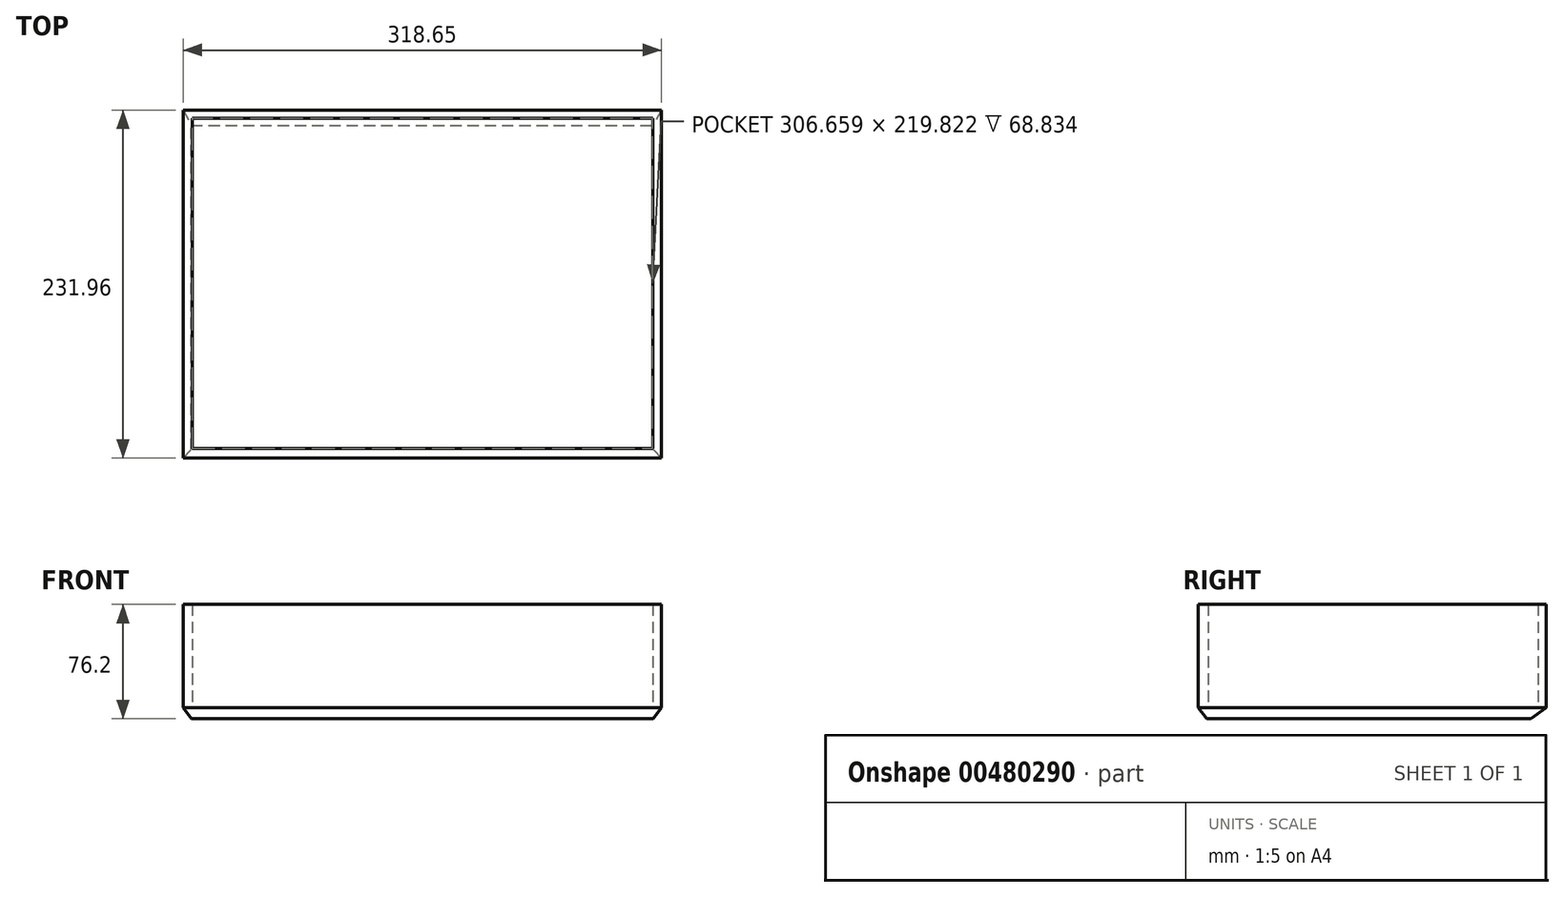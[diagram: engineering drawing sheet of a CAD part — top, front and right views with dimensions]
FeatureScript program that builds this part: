
annotation { "Feature Type Name" : "Feature", "Feature Type Description" : "" }
export const myFeature = defineFeature(function(context is Context, id is Id, definition is map)
    precondition{}
    {
        {
            var Q0;
            Q0=qCreatedBy(makeId("Top.planeOp"),FACE);
            var sketch = newSketch(context, id + "F0", { "sketchPlane" : qUnion([Q0])});
            skLineSegment(sketch, "E0", {"start": v(295, -203.38) * mm, "end": v(-12.7, -203.38) * mm});
            skPoint(sketch, "E1.end.orphan", {"position": v(-12.7, 12.7) * mm});
            skLineSegment(sketch, "E2", {"start": v(-12.7, -203.38) * mm, "end": v(-12.7, 12.7) * mm});
            skLineSegment(sketch, "E3", {"start": v(-12.7, 12.7) * mm, "end": v(295, 12.7) * mm});
            skPoint(sketch, "E4.start.orphan", {"position": v(295, -190.68) * mm});
            skLineSegment(sketch, "E5", {"start": v(295, -203.38) * mm, "end": v(295, 12.7) * mm});
            skPoint(sketch, "E6.end.orphan", {"position": v(0, -190.68) * mm});
            skPoint(sketch, "E7.end.orphan", {"position": v(282.3, -190.68) * mm});
            skPoint(sketch, "E8.start.orphan", {"position": v(0, 0) * mm});
            skSolve(sketch);
        }
        {
            var Q0;
            Q0=qCreatedBy(makeId("Top.planeOp"),FACE);
            cPlane(context, id + "F1", {"entities" : qUnion([Q0]), "cplaneType" : CPlaneType.OFFSET, "offset" : 7.37 * mm, "width" : 152.4 * mm, "height" : 152.4 * mm});
        }
        {
            var Q0;
            Q0=qCreatedBy(id+"F1.planeOp",FACE);
            var sketch = newSketch(context, id + "F2", { "sketchPlane" : qUnion([Q0])});
            skLineSegment(sketch, "E9", {"start": v(-18.2, 22.82) * mm, "end": v(300.45, 22.82) * mm});
            skLineSegment(sketch, "E10", {"start": v(300.45, 22.82) * mm, "end": v(300.45, -209.14) * mm});
            skLineSegment(sketch, "E11", {"start": v(300.45, -209.14) * mm, "end": v(-18.2, -209.14) * mm});
            skLineSegment(sketch, "E12", {"start": v(-18.2, -209.14) * mm, "end": v(-18.2, 22.82) * mm});
            skSolve(sketch);
        }
        {
            var Q0;
            Q0=makeQuery(id+"F2.imprint","IMPRINT",FACE,{"disambiguationData":[TD([[makeQuery(id+"F2.imprint","IMPRINT",EDGE,{"derivedFrom":sQuery(id+"F2.wireOp",EDGE,"E9")}),-1.0]])]});
            var Q1;
            Q1=makeQuery(id+"F0.imprint","IMPRINT",FACE,{"disambiguationData":[TD([[makeQuery(id+"F0.imprint","IMPRINT",EDGE,{"derivedFrom":sQuery(id+"F0.wireOp",EDGE,"E0")}),-1.0]])]});
            loft(context, id + "F3", {"sheetProfilesArray" : [{ "sheetProfileEntities" : qUnion([Q0]) }, { "sheetProfileEntities" : qUnion([Q1]) }]});
        }
        {
            var Q0;
            Q0=makeQuery(id+"F3.opLoft","CAP_FACE",FACE,{"disambiguationData":[OSD([makeQuery(id+"F2.imprint","IMPRINT",FACE,{"disambiguationData":[TD([[makeQuery(id+"F2.imprint","IMPRINT",EDGE,{"derivedFrom":sQuery(id+"F2.wireOp",EDGE,"E9")}),-1.0]])]})])],"isStart":true});
            var sketch = newSketch(context, id + "F4", { "sketchPlane" : qUnion([Q0])});
            skLineSegment(sketch, "E13", {"start": v(-18.2, 22.82) * mm, "end": v(-18.2, -209.14) * mm});
            skLineSegment(sketch, "E14", {"start": v(-18.2, -209.14) * mm, "end": v(300.45, -209.14) * mm});
            skLineSegment(sketch, "E15", {"start": v(300.45, -209.14) * mm, "end": v(300.45, 22.82) * mm});
            skLineSegment(sketch, "E16", {"start": v(300.45, 22.82) * mm, "end": v(-18.2, 22.82) * mm});
            skLineSegment(sketch, "E17", {"start": v(-12.11, 17.28) * mm, "end": v(-12.11, -202.54) * mm});
            skLineSegment(sketch, "E18", {"start": v(-12.11, -202.54) * mm, "end": v(294.55, -202.54) * mm});
            skLineSegment(sketch, "E19", {"start": v(294.55, -202.54) * mm, "end": v(294.55, 17.28) * mm});
            skLineSegment(sketch, "E20", {"start": v(294.55, 17.28) * mm, "end": v(-12.11, 17.28) * mm});
            skSolve(sketch);
        }
        {
            var Q0;
            Q0=makeQuery(id+"F4.imprint","IMPRINT",FACE,{"disambiguationData":[TD([[makeQuery(id+"F4.imprint","IMPRINT",EDGE,{"derivedFrom":sQuery(id+"F4.wireOp",EDGE,"E13")}),-1.0]])]});
            extrude(context, id + "F5", {"entities" : qUnion([Q0]), "operationType" : NewBodyOperationType.ADD, "depth" : 68.83 * mm, "offsetDistance" : 25.4 * mm});
        }
    });
